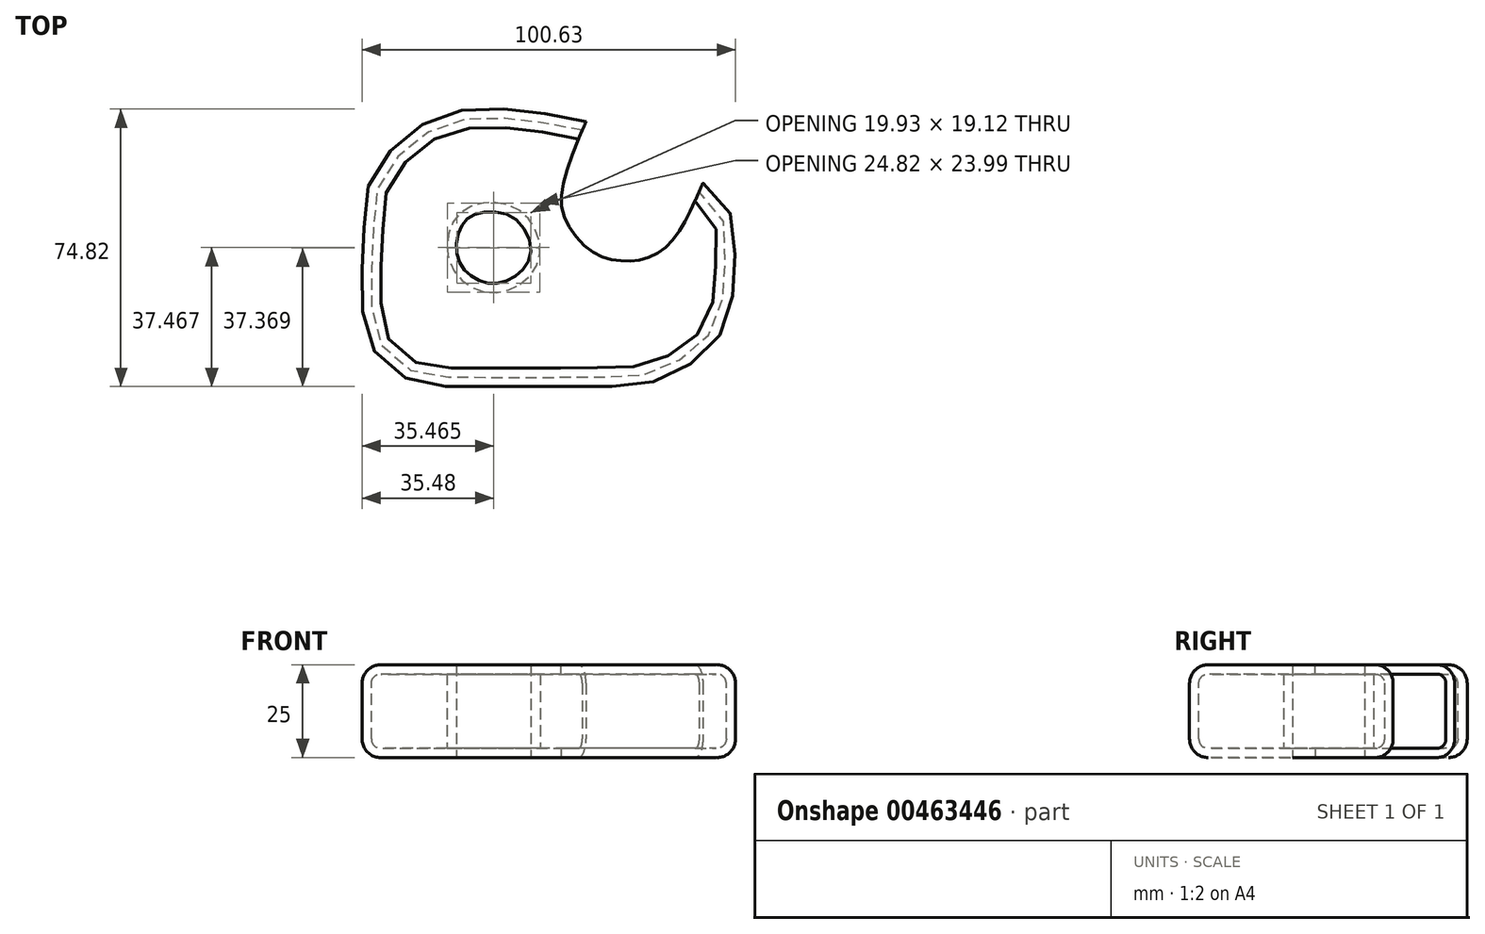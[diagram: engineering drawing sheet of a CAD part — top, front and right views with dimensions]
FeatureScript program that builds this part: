
annotation { "Feature Type Name" : "Feature", "Feature Type Description" : "" }
export const myFeature = defineFeature(function(context is Context, id is Id, definition is map)
    precondition{}
    {
        {
            var Q0;
            Q0=qCreatedBy(makeId("Top.planeOp"),FACE);
            var sketch = newSketch(context, id + "F0", { "sketchPlane" : qUnion([Q0])});
            skFitSpline(sketch, "E0", {"points": [v(-3.24, 38.88) * mm, v(-22.73, 42.1) * mm, v(-33.01, 42.1) * mm, v(-42.83, 40.42) * mm, v(-58.79, 27.68) * mm, v(-62.47, 18.78) * mm, v(-62.93, 12.5) * mm, v(-63.4, -12.52) * mm, v(-59.25, -24.33) * mm, v(-49.73, -31.4) * mm, v(-42.98, -32.46) * mm, v(1.97, -32.46) * mm, v(15.32, -31.08) * mm, v(28.67, -23.57) * mm, v(35.57, -11.75) * mm, v(36.8, 2.52) * mm, v(36.8, 10.65) * mm, v(33.73, 17.25) * mm, v(28.2, 22.31) * mm], "startDerivative": vector(-309.55, 61.97) * mm, "endDerivative": vector(-142.73, 111.57) * mm});
            skFitSpline(sketch, "E1", {"points": [v(28.2, 22.31) * mm, v(23.76, 12.65) * mm, v(18.54, 5.28) * mm, v(11.95, 1.75) * mm, v(5.35, 1.44) * mm, v(-1.71, 3.9) * mm, v(-8.46, 11.72) * mm, v(-9.69, 20.76) * mm, v(-3.24, 38.88) * mm], "startDerivative": vector(-32.65, -75.7) * mm, "endDerivative": vector(48.08, 111.53) * mm});
            skFitSpline(sketch, "E2", {"points": [v(-36.7, 10.96) * mm, v(-38.07, 3.6) * mm, v(-35.16, -1.93) * mm, v(-29.33, -4.7) * mm, v(-22.42, -2.85) * mm, v(-18.13, 3.75) * mm, v(-22.73, 12.95) * mm, v(-31.94, 14.18) * mm, v(-36.7, 10.96) * mm]});
            skSolve(sketch);
        }
        {
            var Q0;
            Q0 = qSketchRegion(id + "F0", true);
            extrude(context, id + "F1", {"entities" : qUnion([Q0]), "depth" : 25 * mm});
        }
        {
            var Q0;
            Q0=makeQuery(id+"F1.opExtrude","CAP_EDGE",EDGE,{"disambiguationData":[OSD([sQuery(id+"F0.wireOp",EDGE,"E0")])],"isStart":true});
            fillet(context, id + "F2", {"entities" : qUnion([Q0]), "radius" : 5 * mm, "tangentPropagation" : true, "allowEdgeOverflow" : false});
        }
        {
            var Q0;
            Q0=makeQuery(id+"F1.opExtrude","CAP_EDGE",EDGE,{"disambiguationData":[OSD([sQuery(id+"F0.wireOp",EDGE,"E0")])],"isStart":false});
            fillet(context, id + "F3", {"entities" : qUnion([Q0]), "radius" : 5 * mm, "tangentPropagation" : true, "allowEdgeOverflow" : false});
        }
        {
            var Q0;
            Q0=makeQuery(id+"F1.opExtrude","SWEPT_FACE",FACE,{"disambiguationData":[OSD([sQuery(id+"F0.wireOp",EDGE,"E1")])]});
            shell(context, id + "F4", {"entities" : qUnion([Q0]), "thickness" : 2.5 * mm});
        }
    });
